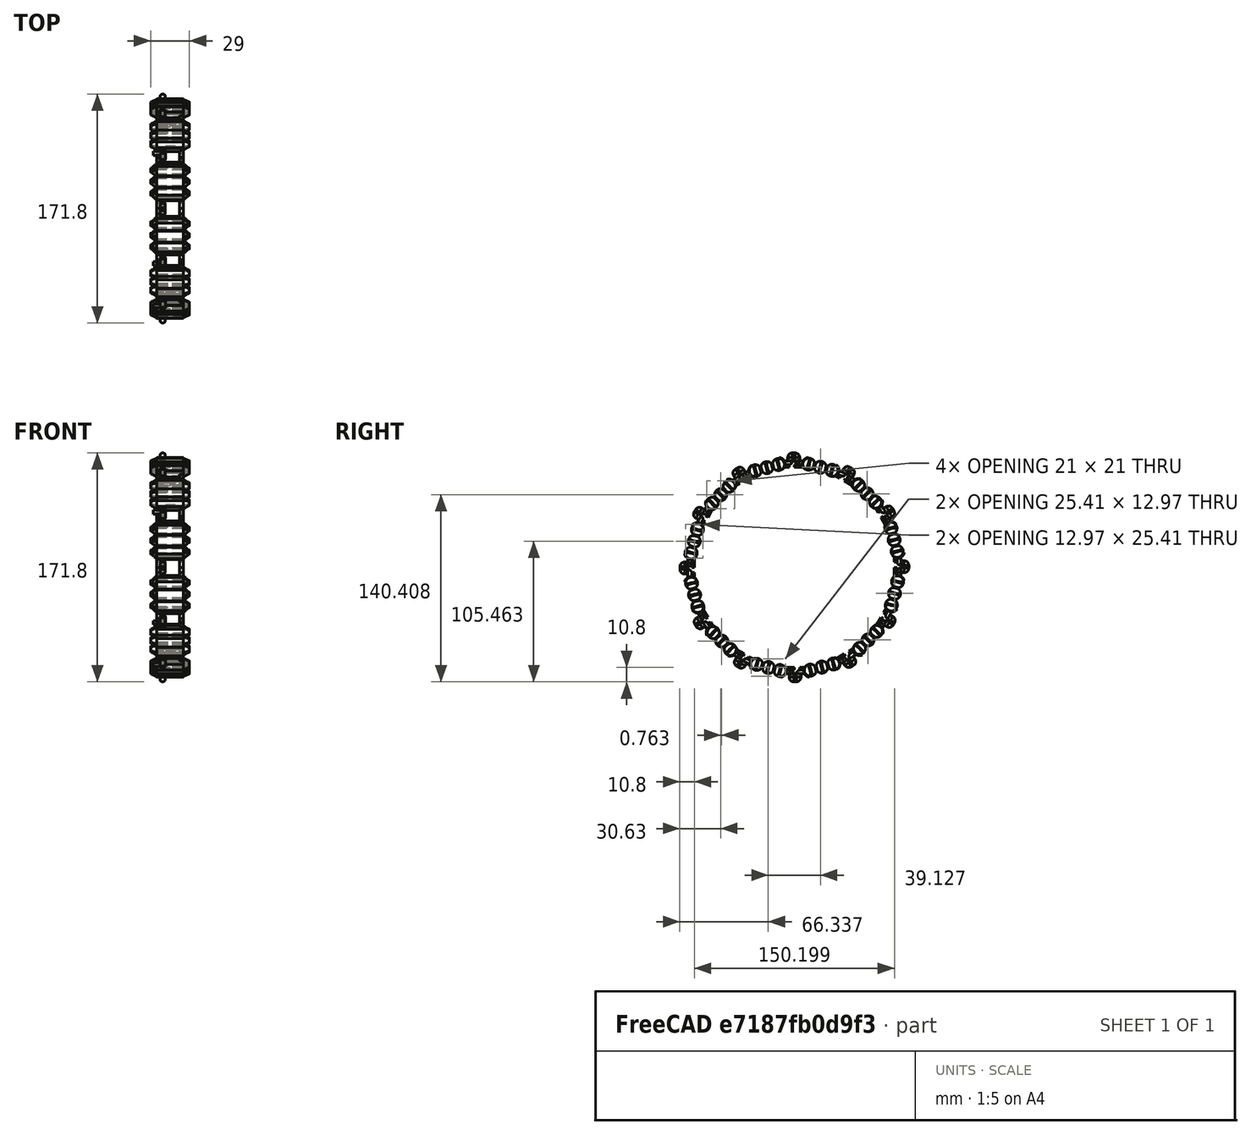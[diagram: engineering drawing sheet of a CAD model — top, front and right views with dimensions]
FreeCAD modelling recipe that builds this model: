
FCSTD DOCUMENT  (FreeCAD 0.19R24291 (Git))
Label: Ring_pneum_act01
License: All rights reserved
LicenseURL: http://en.wikipedia.org/wiki/All_rights_reserved
objects: App::FeaturePython×22, Part::FeaturePython×17
note: 17 computed .brp shape members not serialized (recipe doc carries the construction recipe); baked Part::Feature solids carry a one-line shape summary decoded from their .brp

FEATURE [Part::FeaturePython] b_shell_chamb12_001_  label="shell_chamb12_001"  # a2plus imported part (geometry in sourceFile) (typed FeaturePython)
  Placement = pos=(0,0,-15) rot=(0,0,1;0rad)
  a2p_Version = V0.1
  fixedPosition = true
  objectType = a2pPart
  sourceFile = ./../cod/design CAD/shell_chamb12.FCStd
  subassemblyImport = false
  timeLastImport = 1.65081e+09
  updateColors = true
FEATURE [Part::FeaturePython] b_actuator8_piston_001_  label="actuator8_piston_001"  # a2plus imported part (geometry in sourceFile) (typed FeaturePython)
  Placement = pos=(-10,-9.9851,1.42353) rot=(0,0,1;0rad)
  a2p_Version = V0.1
  fixedPosition = false
  objectType = a2pPart
  sourceFile = ./../cod/design CAD/actuator8_piston.FCStd
  subassemblyImport = false
  timeLastImport = 1.65029e+09
  updateColors = true
FEATURE [App::FeaturePython] axisCoincident_001  label="axisCoincident_001__actuator8_piston_001"  # a2plus constraint (typed FeaturePython)
  Object1 = b_shell_chamb12_001_
  Object2 = b_actuator8_piston_001_
  ParentTreeObject = -> b_shell_chamb12_001_
  SubElement1 = Edge93
  SubElement2 = Edge66
  Suppressed = false
  Type = axial
  directionConstraint = 0
  lockRotation = false
FEATURE [App::FeaturePython] axisCoincident_001_mirror  label="axisCoincident_001__shell_chamb12_001"  # a2plus constraint (typed FeaturePython)
  Object1 = b_shell_chamb12_001_
  Object2 = b_actuator8_piston_001_
  ParentTreeObject = -> b_actuator8_piston_001_
  SubElement1 = Edge93
  SubElement2 = Edge66
  Suppressed = false
  Type = axial
  directionConstraint = 0
  lockRotation = false
FEATURE [App::FeaturePython] axisCoincident_002  label="axisCoincident_002__actuator8_piston_001"  # a2plus constraint (typed FeaturePython)
  Object1 = b_shell_chamb12_001_
  Object2 = b_actuator8_piston_001_
  ParentTreeObject = -> b_shell_chamb12_001_
  SubElement1 = Edge19
  SubElement2 = Edge53
  Suppressed = false
  Type = axial
  directionConstraint = 1
  lockRotation = false
FEATURE [App::FeaturePython] axisCoincident_002_mirror  label="axisCoincident_002__shell_chamb12_001"  # a2plus constraint (typed FeaturePython)
  Object1 = b_shell_chamb12_001_
  Object2 = b_actuator8_piston_001_
  ParentTreeObject = -> b_actuator8_piston_001_
  SubElement1 = Edge19
  SubElement2 = Edge53
  Suppressed = false
  Type = axial
  directionConstraint = 1
  lockRotation = false
FEATURE [Part::FeaturePython] b_actuator8_pistonPCBside_001_  label="actuator8_pistonPCBside_001"  # a2plus imported part (geometry in sourceFile) (typed FeaturePython)
  Placement = pos=(10,12.9851,1.42353) rot=(0,0,1;3.14159rad)
  a2p_Version = V0.1
  fixedPosition = false
  objectType = a2pPart
  sourceFile = ./../cod/design CAD/actuator8_pistonPCBside.FCStd
  subassemblyImport = false
  timeLastImport = 1.65029e+09
  updateColors = true
FEATURE [App::FeaturePython] axisCoincident_003  label="axisCoincident_003__actuator8_pistonPCBside_001"  # a2plus constraint (typed FeaturePython)
  Object1 = b_shell_chamb12_001_
  Object2 = b_actuator8_pistonPCBside_001_
  ParentTreeObject = -> b_shell_chamb12_001_
  SubElement1 = Edge24
  SubElement2 = Edge66
  Suppressed = false
  Type = axial
  directionConstraint = 0
  lockRotation = false
FEATURE [App::FeaturePython] axisCoincident_003_mirror  label="axisCoincident_003__shell_chamb12_001"  # a2plus constraint (typed FeaturePython)
  Object1 = b_shell_chamb12_001_
  Object2 = b_actuator8_pistonPCBside_001_
  ParentTreeObject = -> b_actuator8_pistonPCBside_001_
  SubElement1 = Edge24
  SubElement2 = Edge66
  Suppressed = false
  Type = axial
  directionConstraint = 0
  lockRotation = false
FEATURE [App::FeaturePython] axisCoincident_004  label="axisCoincident_004__actuator8_pistonPCBside_001"  # a2plus constraint (typed FeaturePython)
  Object1 = b_shell_chamb12_001_
  Object2 = b_actuator8_pistonPCBside_001_
  ParentTreeObject = -> b_shell_chamb12_001_
  SubElement1 = Edge58
  SubElement2 = Edge51
  Suppressed = false
  Type = axial
  directionConstraint = 1
  lockRotation = false
FEATURE [App::FeaturePython] axisCoincident_004_mirror  label="axisCoincident_004__shell_chamb12_001"  # a2plus constraint (typed FeaturePython)
  Object1 = b_shell_chamb12_001_
  Object2 = b_actuator8_pistonPCBside_001_
  ParentTreeObject = -> b_actuator8_pistonPCBside_001_
  SubElement1 = Edge58
  SubElement2 = Edge51
  Suppressed = false
  Type = axial
  directionConstraint = 1
  lockRotation = false
FEATURE [Part::FeaturePython] b_bush_simply02_001_  label="bush_simply02_001"  # a2plus imported part (geometry in sourceFile) (typed FeaturePython)
  Placement = pos=(-5.5,-0.999959,3.92149) rot=(0,0,1;1.5708rad)
  a2p_Version = V0.1
  fixedPosition = false
  objectType = a2pPart
  sourceFile = ./../cod/design CAD/bush_simply02.FCStd
  subassemblyImport = false
  timeLastImport = 1.65037e+09
  updateColors = true
FEATURE [App::FeaturePython] pointIdentity_001  label="pointIdentity_001__bush_simply02_001"  # a2plus constraint (typed FeaturePython)
  Object1 = b_actuator8_pistonPCBside_001_
  Object2 = b_bush_simply02_001_
  ParentTreeObject = -> b_actuator8_pistonPCBside_001_
  SubElement1 = Edge71
  SubElement2 = Edge13
  Suppressed = false
  Type = pointIdentity
FEATURE [App::FeaturePython] pointIdentity_001_mirror  label="pointIdentity_001__actuator8_pistonPCBside_001"  # a2plus constraint (typed FeaturePython)
  Object1 = b_actuator8_pistonPCBside_001_
  Object2 = b_bush_simply02_001_
  ParentTreeObject = -> b_bush_simply02_001_
  SubElement1 = Edge71
  SubElement2 = Edge13
  Suppressed = false
  Type = pointIdentity
FEATURE [Part::FeaturePython] b_actuator8_001_  label="actuator8_001"  # a2plus imported part (geometry in sourceFile) (typed FeaturePython)
  Placement = pos=(-9.988,21.5271,-0.87159) rot=(-0.129428,0.129428,0.983106;1.58783rad)
  a2p_Version = V0.1
  fixedPosition = false
  objectType = a2pPart
  sourceFile = ./../cod/design CAD/actuator8.FCStd
  subassemblyImport = false
  timeLastImport = 1.64676e+09
  updateColors = true
FEATURE [Part::FeaturePython] b_actuator8_side_001_  label="actuator8_side_001"  # a2plus imported part (geometry in sourceFile) (typed FeaturePython)
  Placement = pos=(10.012,21.5547,-0.878988) rot=(-0.129428,0.129428,0.983106;1.58783rad)
  a2p_Version = V0.1
  fixedPosition = false
  objectType = a2pPart
  sourceFile = ./../cod/design CAD/actuator8_side.FCStd
  subassemblyImport = false
  timeLastImport = 1.6469e+09
  updateColors = true
FEATURE [App::FeaturePython] planesParallel_001  label="planesParallel_001__actuator8_001"  # a2plus constraint (typed FeaturePython)
  Object1 = b_actuator8_pistonPCBside_001_
  Object2 = b_actuator8_001_
  ParentTreeObject = -> b_actuator8_pistonPCBside_001_
  SubElement1 = Face4
  SubElement2 = Face5
  Suppressed = false
  Type = planesParallel
  directionConstraint = 0
FEATURE [App::FeaturePython] planesParallel_001_mirror  label="planesParallel_001__actuator8_pistonPCBside_001"  # a2plus constraint (typed FeaturePython)
  Object1 = b_actuator8_pistonPCBside_001_
  Object2 = b_actuator8_001_
  ParentTreeObject = -> b_actuator8_001_
  SubElement1 = Face4
  SubElement2 = Face5
  Suppressed = false
  Type = planesParallel
  directionConstraint = 0
FEATURE [App::FeaturePython] axisParallel_001  label="axisParallel_001__actuator8_001"  # a2plus constraint (typed FeaturePython)
  Object1 = b_actuator8_pistonPCBside_001_
  Object2 = b_actuator8_001_
  ParentTreeObject = -> b_actuator8_pistonPCBside_001_
  SubElement1 = Edge11
  SubElement2 = Edge58
  Suppressed = false
  Type = axisParallel
  directionConstraint = 1
FEATURE [App::FeaturePython] axisParallel_001_mirror  label="axisParallel_001__actuator8_pistonPCBside_001"  # a2plus constraint (typed FeaturePython)
  Object1 = b_actuator8_pistonPCBside_001_
  Object2 = b_actuator8_001_
  ParentTreeObject = -> b_actuator8_001_
  SubElement1 = Edge11
  SubElement2 = Edge58
  Suppressed = false
  Type = axisParallel
  directionConstraint = 1
FEATURE [App::FeaturePython] axisCoincident_005  label="axisCoincident_005__actuator8_side_001"  # a2plus constraint (typed FeaturePython)
  Object1 = b_actuator8_001_
  Object2 = b_actuator8_side_001_
  ParentTreeObject = -> b_actuator8_001_
  SubElement1 = Edge24
  SubElement2 = Edge18
  Suppressed = false
  Type = axial
  directionConstraint = 0
  lockRotation = false
FEATURE [App::FeaturePython] axisCoincident_005_mirror  label="axisCoincident_005__actuator8_001"  # a2plus constraint (typed FeaturePython)
  Object1 = b_actuator8_001_
  Object2 = b_actuator8_side_001_
  ParentTreeObject = -> b_actuator8_side_001_
  SubElement1 = Edge24
  SubElement2 = Edge18
  Suppressed = false
  Type = axial
  directionConstraint = 0
  lockRotation = false
FEATURE [App::FeaturePython] planeCoincident_001  label="planeCoincident_001__actuator8_side_001"  # a2plus constraint (typed FeaturePython)
  Object1 = b_actuator8_001_
  Object2 = b_actuator8_side_001_
  ParentTreeObject = -> b_actuator8_001_
  SubElement1 = Face5
  SubElement2 = Face3
  Suppressed = false
  Type = plane
  directionConstraint = 0
  offset = 0
FEATURE [App::FeaturePython] planeCoincident_001_mirror  label="planeCoincident_001__actuator8_001"  # a2plus constraint (typed FeaturePython)
  Object1 = b_actuator8_001_
  Object2 = b_actuator8_side_001_
  ParentTreeObject = -> b_actuator8_side_001_
  SubElement1 = Face5
  SubElement2 = Face3
  Suppressed = false
  Type = plane
  directionConstraint = 0
  offset = 0
FEATURE [Part::FeaturePython] b_actuator8_side_001_001  label="actuator8_side_002"  # a2plus imported part (geometry in sourceFile) (typed FeaturePython)
  Placement = pos=(-9.98801,21.5209,-0.869941) rot=(-0.129428,-0.129428,-0.983106;1.58783rad)
  a2p_Version = V0.1
  fixedPosition = false
  objectType = a2pPart
  sourceFile = ./../cod/design CAD/actuator8_side.FCStd
  subassemblyImport = false
  timeLastImport = 1.6469e+09
  updateColors = true
FEATURE [App::FeaturePython] axisCoincident_006  label="axisCoincident_006__actuator8_side_002"  # a2plus constraint (typed FeaturePython)
  Object1 = b_actuator8_001_
  Object2 = b_actuator8_side_001_001
  ParentTreeObject = -> b_actuator8_001_
  SubElement1 = Edge11
  SubElement2 = Edge79
  Suppressed = false
  Type = axial
  directionConstraint = 1
  lockRotation = false
FEATURE [App::FeaturePython] axisCoincident_006_mirror  label="axisCoincident_006__actuator8_001"  # a2plus constraint (typed FeaturePython)
  Object1 = b_actuator8_001_
  Object2 = b_actuator8_side_001_001
  ParentTreeObject = -> b_actuator8_side_001_001
  SubElement1 = Edge11
  SubElement2 = Edge79
  Suppressed = false
  Type = axial
  directionConstraint = 1
  lockRotation = false
FEATURE [App::FeaturePython] planeCoincident_002  label="planeCoincident_002__actuator8_side_002"  # a2plus constraint (typed FeaturePython)
  Object1 = b_actuator8_001_
  Object2 = b_actuator8_side_001_001
  ParentTreeObject = -> b_actuator8_001_
  SubElement1 = Face4
  SubElement2 = Face27
  Suppressed = false
  Type = plane
  directionConstraint = 1
  offset = 0
FEATURE [App::FeaturePython] planeCoincident_002_mirror  label="planeCoincident_002__actuator8_001"  # a2plus constraint (typed FeaturePython)
  Object1 = b_actuator8_001_
  Object2 = b_actuator8_side_001_001
  ParentTreeObject = -> b_actuator8_side_001_001
  SubElement1 = Face4
  SubElement2 = Face27
  Suppressed = false
  Type = plane
  directionConstraint = 1
  offset = 0
FEATURE [Part::FeaturePython] Array  # Draft array (typed FeaturePython)
  Angle = 360
  ArrayType = 1
  Axis = (1,0,0)
  Base = -> b_actuator8_piston_001_
  Center = (0,2,-76)
  Count = 12
  ExpandArray = false
  Fuse = true
  IntervalAxis = (0,0,0)
  IntervalX = (50,0,0)
  IntervalY = (0,50,0)
  IntervalZ = (0,0,50)
  NumberCircles = 3
  NumberPolar = 12
  NumberX = 2
  NumberY = 2
  NumberZ = 1
  PlacementList = 12 placements: [(-10,-9.9851,1.42353),(-10,-47.0912,-14.9418),(-10,-71.0433,-47.6676),(-10,-75.4235,-87.9851),(-10,-59.0582,-125.091),(-10,-26.3324,-149.043),(-10,13.9851,-153.424),(-10,51.0912,-137.058),(-10,75.0433,-104.332),(-10,79.4235,-64.0149),(-10,63.0582,-26.9088),(-10,30.3324,-2.95671)]
  RadialDistance = 50
  ScaleList = (12) [(1,1,1),(1,1,1),(1,1,1),(1,1,1),(1,1,1),(1,1,1),(1,1,1),(1,1,1),(1,1,1),(1,1,1),(1,1,1),(1,1,1)]
  Symmetry = 1
  TangentialDistance = 25
FEATURE [Part::FeaturePython] Array001  # Draft array (typed FeaturePython)
  Angle = 360
  ArrayType = 1
  Axis = (1,0,0)
  Base = -> b_actuator8_pistonPCBside_001_
  Center = (0,2,-76)
  Count = 12
  ExpandArray = false
  Fuse = true
  IntervalAxis = (0,0,0)
  IntervalX = (50,0,0)
  IntervalY = (0,50,0)
  IntervalZ = (0,0,50)
  NumberCircles = 3
  NumberPolar = 12
  NumberX = 2
  NumberY = 2
  NumberZ = 1
  PlacementList = 12 placements: [(10,12.9851,1.42353),(10,-27.1984,-3.45671),(10,-59.5582,-27.7749),(10,-75.4235,-65.0149),(10,-70.5433,-105.198),(10,-46.2251,-137.558),(10,-8.9851,-153.424),(10,31.1984,-148.543),(10,63.5582,-124.225),(10,79.4235,-86.9851),(10,74.5433,-46.8016),(10,50.2251,-14.4418)]
  RadialDistance = 50
  ScaleList = (12) [(1,1,1),(1,1,1),(1,1,1),(1,1,1),(1,1,1),(1,1,1),(1,1,1),(1,1,1),(1,1,1),(1,1,1),(1,1,1),(1,1,1)]
  Symmetry = 1
  TangentialDistance = 25
FEATURE [Part::FeaturePython] Array002  # Draft array (typed FeaturePython)
  Angle = 360
  ArrayType = 1
  Axis = (1,0,0)
  Base = -> b_actuator8_001_
  Center = (0,2,-76)
  Count = 12
  ExpandArray = false
  Fuse = true
  IntervalAxis = (0,0,0)
  IntervalX = (50,0,0)
  IntervalY = (0,50,0)
  IntervalZ = (0,0,50)
  NumberCircles = 3
  NumberPolar = 12
  NumberX = 2
  NumberY = 2
  NumberZ = 1
  PlacementList = 12 placements: [(-9.988,21.5271,-0.87159),(-9.988,-18.6533,-1.17335),(-9.988,-53.2996,-21.5249),(-9.988,-73.1284,-56.4729),(-9.988,-72.8266,-96.6533),(-9.988,-52.4751,-131.3),(-9.988,-17.5271,-151.128),(-9.988,22.6533,-150.827),(-9.988,57.2996,-130.475),(-9.988,77.1284,-95.5271),(-9.988,76.8266,-55.3467),(-9.988,56.4751,-20.7004)]
  RadialDistance = 50
  ScaleList = (12) [(1,1,1),(1,1,1),(1,1,1),(1,1,1),(1,1,1),(1,1,1),(1,1,1),(1,1,1),(1,1,1),(1,1,1),(1,1,1),(1,1,1)]
  Symmetry = 1
  TangentialDistance = 25
FEATURE [Part::FeaturePython] Array003  # Draft array (typed FeaturePython)
  Angle = 360
  ArrayType = 1
  Axis = (1,0,0)
  Base = -> b_actuator8_side_001_
  Center = (0,2,-76)
  Count = 12
  ExpandArray = false
  Fuse = true
  IntervalAxis = (0,0,0)
  IntervalX = (50,0,0)
  IntervalY = (0,50,0)
  IntervalZ = (0,0,50)
  NumberCircles = 3
  NumberPolar = 12
  NumberX = 2
  NumberY = 2
  NumberZ = 1
  PlacementList = 12 placements: [(10.012,21.5547,-0.878988),(10.012,-18.6257,-1.16595),(10.012,-53.2794,-21.5046),(10.012,-73.121,-56.4453),(10.012,-72.834,-96.6257),(10.012,-52.4954,-131.279),(10.012,-17.5547,-151.121),(10.012,22.6257,-150.834),(10.012,57.2794,-130.495),(10.012,77.121,-95.5547),(10.012,76.834,-55.3743),(10.012,56.4954,-20.7206)]
  RadialDistance = 50
  ScaleList = (12) [(1,1,1),(1,1,1),(1,1,1),(1,1,1),(1,1,1),(1,1,1),(1,1,1),(1,1,1),(1,1,1),(1,1,1),(1,1,1),(1,1,1)]
  Symmetry = 1
  TangentialDistance = 25
FEATURE [Part::FeaturePython] Array004  # Draft array (typed FeaturePython)
  Angle = 360
  ArrayType = 1
  Axis = (1,0,0)
  Base = -> b_actuator8_side_001_001
  Center = (0,2,-76)
  Count = 12
  ExpandArray = false
  Fuse = true
  IntervalAxis = (0,0,0)
  IntervalX = (50,0,0)
  IntervalY = (0,50,0)
  IntervalZ = (0,0,50)
  NumberCircles = 3
  NumberPolar = 12
  NumberX = 2
  NumberY = 2
  NumberZ = 1
  PlacementList = 12 placements: [(-9.98801,21.5209,-0.869941),(-9.98801,-18.6594,-1.175),(-9.98801,-53.3041,-21.5294),(-9.98801,-73.1301,-56.4791),(-9.98801,-72.825,-96.6594),(-9.98801,-52.4706,-131.304),(-9.98801,-17.5209,-151.13),(-9.98801,22.6594,-150.825),(-9.98801,57.3041,-130.471),(-9.98801,77.1301,-95.5209),(-9.98801,76.825,-55.3406),(-9.98801,56.4706,-20.6959)]
  RadialDistance = 50
  ScaleList = (12) [(1,1,1),(1,1,1),(1,1,1),(1,1,1),(1,1,1),(1,1,1),(1,1,1),(1,1,1),(1,1,1),(1,1,1),(1,1,1),(1,1,1)]
  Symmetry = 1
  TangentialDistance = 25
FEATURE [Part::FeaturePython] b_bush_feeder03_001_  label="bush_feeder03_001"  # a2plus imported part (geometry in sourceFile) (typed FeaturePython)
  Placement = pos=(-5.44609,43.6368,-7.73811) rot=(-0.250563,-0.250563,-0.935113;1.63783rad)
  a2p_Version = V0.1
  fixedPosition = false
  objectType = a2pPart
  sourceFile = ./../cod/design CAD/bush_feeder03.FCStd
  subassemblyImport = false
  timeLastImport = 1.65054e+09
  updateColors = true
FEATURE [Part::FeaturePython] b_bush_simply02_001_001  label="bush_simply02_002"  # a2plus imported part (geometry in sourceFile) (typed FeaturePython)
  Placement = pos=(-5.52065,-36.3086,-5.69944) rot=(0.250563,0.250563,-0.935113;1.63783rad)
  a2p_Version = V0.1
  fixedPosition = false
  objectType = a2pPart
  sourceFile = ./../cod/design CAD/bush_simply02.FCStd
  subassemblyImport = false
  timeLastImport = 1.65037e+09
  updateColors = true
FEATURE [Part::FeaturePython] Array005  # Draft array (typed FeaturePython)
  Angle = 360
  ArrayType = 1
  Axis = (1,0,0)
  Base = -> b_bush_simply02_001_
  Center = (0,2,-76)
  Count = 4
  ExpandArray = false
  Fuse = true
  IntervalAxis = (0,0,0)
  IntervalX = (50,0,0)
  IntervalY = (0,50,0)
  IntervalZ = (0,0,50)
  NumberCircles = 3
  NumberPolar = 4
  NumberX = 2
  NumberY = 2
  NumberZ = 1
  PlacementList = 4 placements: [(-5.5,-0.999959,3.92149),(-5.5,-77.9215,-79),(-5.5,4.99996,-155.921),(-5.5,81.9215,-73)]
  RadialDistance = 50
  ScaleList = (4) [(1,1,1),(1,1,1),(1,1,1),(1,1,1)]
  Symmetry = 1
  TangentialDistance = 25
FEATURE [Part::FeaturePython] Array006  # Draft array (typed FeaturePython)
  Angle = 360
  ArrayType = 1
  Axis = (1,0,0)
  Base = -> b_bush_feeder03_001_
  Center = (0,2,-76)
  Count = 4
  ExpandArray = false
  Fuse = true
  IntervalAxis = (0,0,0)
  IntervalX = (50,0,0)
  IntervalY = (0,50,0)
  IntervalZ = (0,0,50)
  NumberCircles = 3
  NumberPolar = 4
  NumberX = 2
  NumberY = 2
  NumberZ = 1
  PlacementList = 4 placements: [(-5.44609,43.6368,-7.73811),(-5.44609,-66.2619,-34.3632),(-5.44609,-39.6368,-144.262),(-5.44609,70.2619,-117.637)]
  RadialDistance = 50
  ScaleList = (4) [(1,1,1),(1,1,1),(1,1,1),(1,1,1)]
  Symmetry = 1
  TangentialDistance = 25
FEATURE [Part::FeaturePython] Array007  # Draft array (typed FeaturePython)
  Angle = 360
  ArrayType = 1
  Axis = (1,0,0)
  Base = -> b_bush_simply02_001_001
  Center = (0,2,-76)
  Count = 4
  ExpandArray = false
  Fuse = true
  IntervalAxis = (0,0,0)
  IntervalX = (50,0,0)
  IntervalY = (0,50,0)
  IntervalZ = (0,0,50)
  NumberCircles = 3
  NumberPolar = 4
  NumberX = 2
  NumberY = 2
  NumberZ = 1
  PlacementList = 4 placements: [(-5.52065,-36.3086,-5.69944),(-5.52065,-68.3006,-114.309),(-5.52065,40.3086,-146.301),(-5.52065,72.3006,-37.6914)]
  RadialDistance = 50
  ScaleList = (4) [(1,1,1),(1,1,1),(1,1,1),(1,1,1)]
  Symmetry = 1
  TangentialDistance = 25
